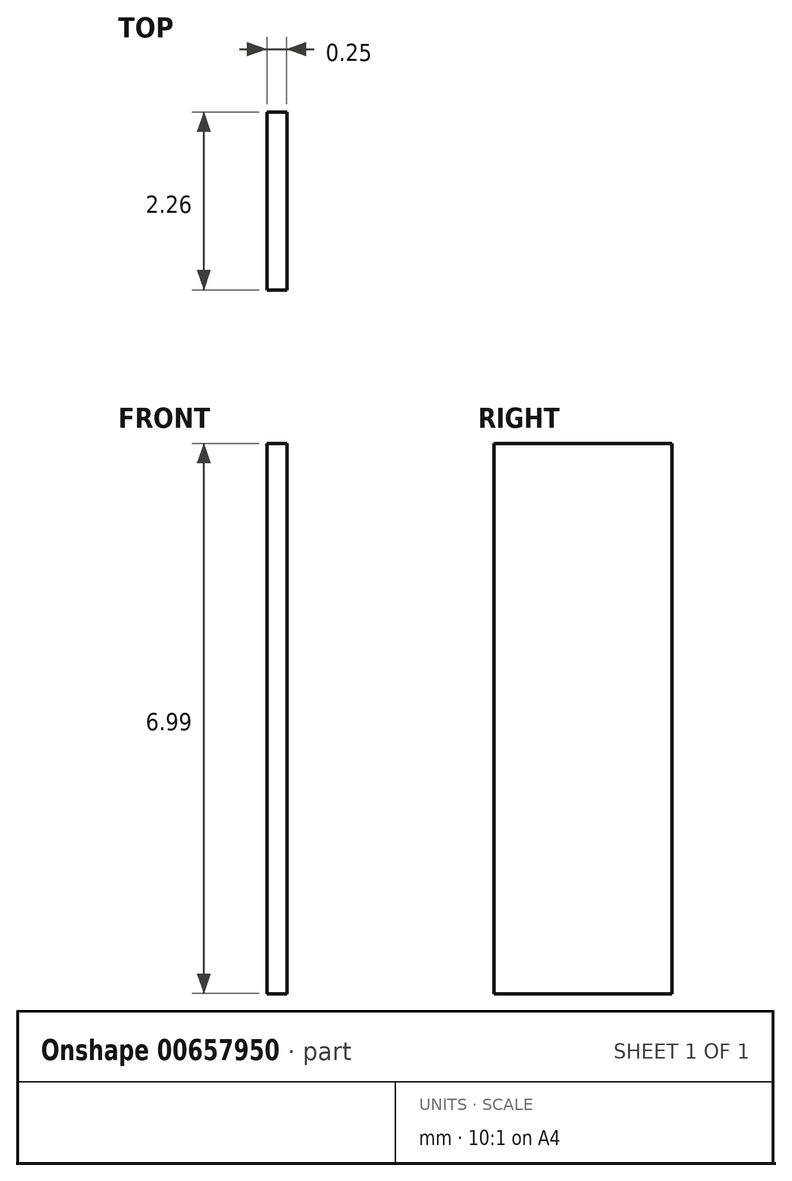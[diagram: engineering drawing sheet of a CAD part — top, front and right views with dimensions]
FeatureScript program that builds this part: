
annotation { "Feature Type Name" : "Feature", "Feature Type Description" : "" }
export const myFeature = defineFeature(function(context is Context, id is Id, definition is map)
    precondition{}
    {
        {
            var Q0;
            Q0=qCreatedBy(makeId("Right.planeOp"),FACE);
            var sketch = newSketch(context, id + "F0", { "sketchPlane" : qUnion([Q0])});
            skLineSegment(sketch, "E0", {"start": v(-57.95, 47.9) * mm, "end": v(-57.95, 36) * mm});
            skSolve(sketch);
        }
        {
            var Q0;
            Q0=sQuery(id+"F0.wireOp",EDGE,"E0");
            extrude(context, id + "F1", {"bodyType" : ToolBodyType.SURFACE, "surfaceEntities" : qUnion([Q0]), "depth" : 0.25 * mm, "offsetDistance" : 25.4 * mm});
        }
        {
            var Q0;
            Q0=qCreatedBy(makeId("Right.planeOp"),FACE);
            var sketch = newSketch(context, id + "F2", { "sketchPlane" : qUnion([Q0])});
            skLineSegment(sketch, "E1.bottom", {"start": v(-324.98, 297.52) * mm, "end": v(-322.72, 297.52) * mm});
            skLineSegment(sketch, "E1.top", {"start": v(-324.98, 290.53) * mm, "end": v(-322.72, 290.53) * mm});
            skLineSegment(sketch, "E1.left", {"start": v(-324.98, 297.52) * mm, "end": v(-324.98, 290.53) * mm});
            skLineSegment(sketch, "E1.right", {"start": v(-322.72, 297.52) * mm, "end": v(-322.72, 290.53) * mm});
            skSolve(sketch);
        }
        {
            var Q0;
            Q0=makeQuery(id+"F2.imprint","IMPRINT",FACE,{"disambiguationData":[TD([[makeQuery(id+"F2.imprint","IMPRINT",EDGE,{"derivedFrom":sQuery(id+"F2.wireOp",EDGE,"E1.bottom")}),-1.0]])]});
            extrude(context, id + "F3", {"entities" : qUnion([Q0]), "depth" : 0.25 * mm, "offsetDistance" : 25.4 * mm});
        }
    });
